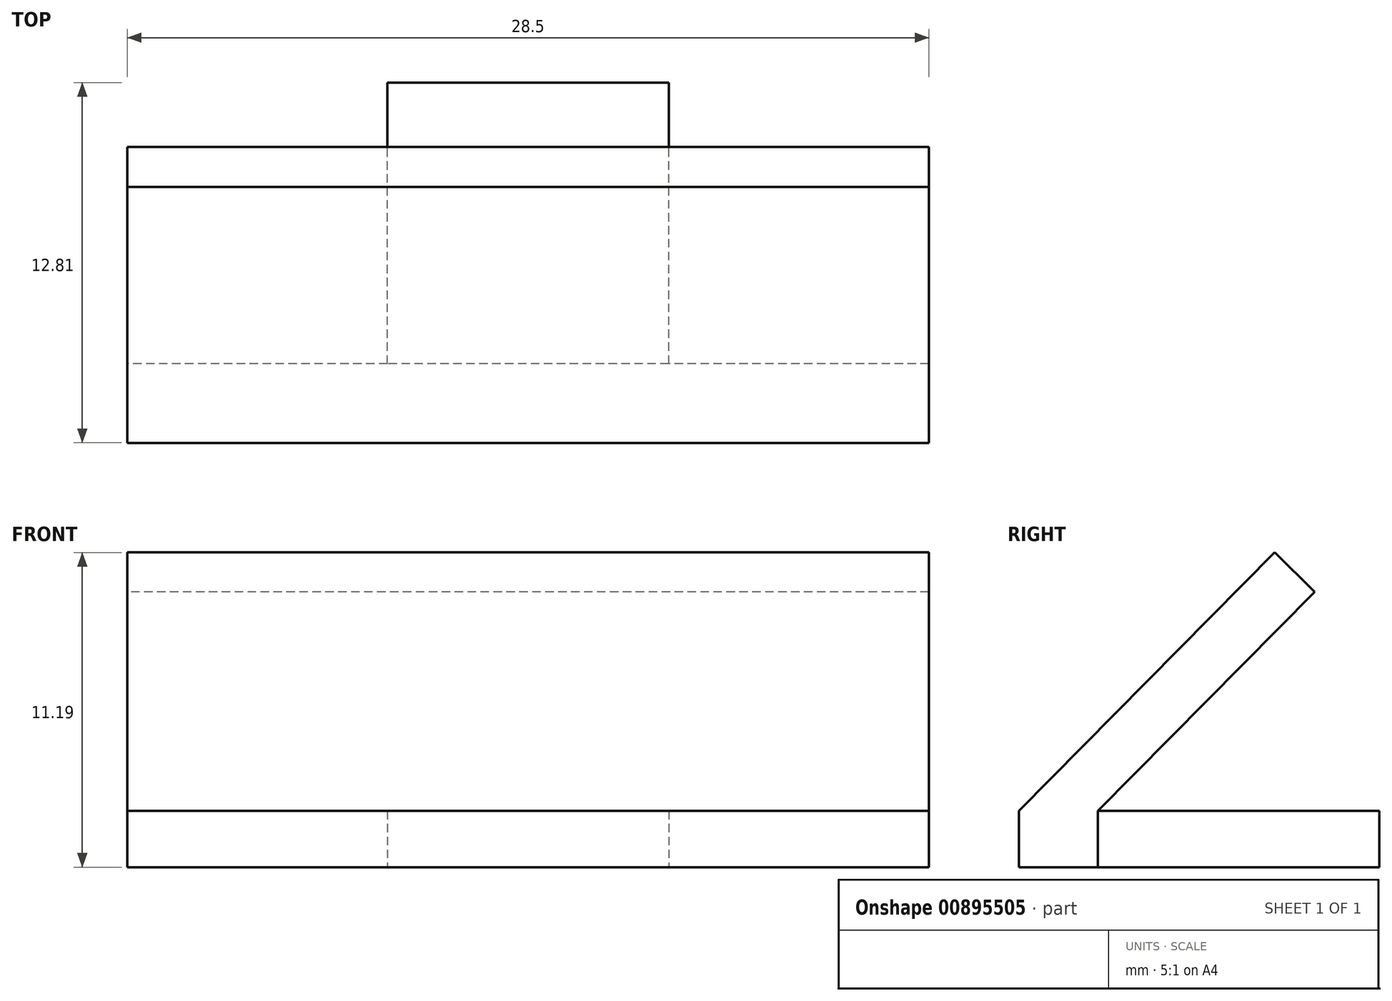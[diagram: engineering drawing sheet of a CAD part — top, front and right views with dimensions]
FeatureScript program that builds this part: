
annotation { "Feature Type Name" : "Feature", "Feature Type Description" : "" }
export const myFeature = defineFeature(function(context is Context, id is Id, definition is map)
    precondition{}
    {
        {
            var Q0;
            Q0=qCreatedBy(makeId("Top.planeOp"),FACE);
            var sketch = newSketch(context, id + "F0", { "sketchPlane" : qUnion([Q0])});
            skLineSegment(sketch, "E0.bottom", {"start": v(5, -5) * mm, "end": v(-5, -5) * mm});
            skLineSegment(sketch, "E0.top", {"start": v(5, 5) * mm, "end": v(-5, 5) * mm});
            skLineSegment(sketch, "E0.left", {"start": v(5, -5) * mm, "end": v(5, 5) * mm});
            skLineSegment(sketch, "E0.right", {"start": v(-5, -5) * mm, "end": v(-5, 5) * mm});
            skPoint(sketch, "E0.middle", {"position": v(0, 0) * mm});
            skSolve(sketch);
        }
        {
            var Q0;
            Q0 = qSketchRegion(id + "F0", true);
            extrude(context, id + "F1", {"entities" : qUnion([Q0]), "depth" : 2 * mm, "offsetDistance" : 25 * mm});
        }
        {
            var Q0;
            Q0=qCreatedBy(makeId("Right.planeOp"),FACE);
            var sketch = newSketch(context, id + "F2", { "sketchPlane" : qUnion([Q0])});
            skPoint(sketch, "E1.0", {"position": v(-5, 2) * mm});
            skPoint(sketch, "E1.1", {"position": v(-5, 0) * mm});
            skPoint(sketch, "E1.2", {"position": v(5, 2) * mm});
            skPoint(sketch, "E1.3", {"position": v(5, 0) * mm});
            skPoint(sketch, "E1.4", {"position": v(0, 2) * mm});
            skLineSegment(sketch, "E2", {"start": v(-5, 2) * mm, "end": v(2.7, 9.78) * mm});
            skLineSegment(sketch, "E3", {"start": v(2.7, 9.78) * mm, "end": v(1.29, 11.2) * mm});
            skLineSegment(sketch, "E4", {"start": v(1.29, 11.2) * mm, "end": v(-7.81, 2) * mm});
            skLineSegment(sketch, "E5", {"start": v(-7.81, 2) * mm, "end": v(-7.81, 0) * mm});
            skLineSegment(sketch, "E6", {"start": v(-7.81, 0) * mm, "end": v(-5, 0) * mm});
            skLineSegment(sketch, "E7", {"start": v(-5, 2) * mm, "end": v(-5, 0) * mm});
            skSolve(sketch);
        }
        {
            var Q0;
            Q0 = qSketchRegion(id + "F2", true);
            extrude(context, id + "F3", {"entities" : qUnion([Q0]), "operationType" : NewBodyOperationType.ADD, "depth" : 28.5 * mm, "offsetDistance" : 25 * mm, "symmetric" : true});
        }
    });
